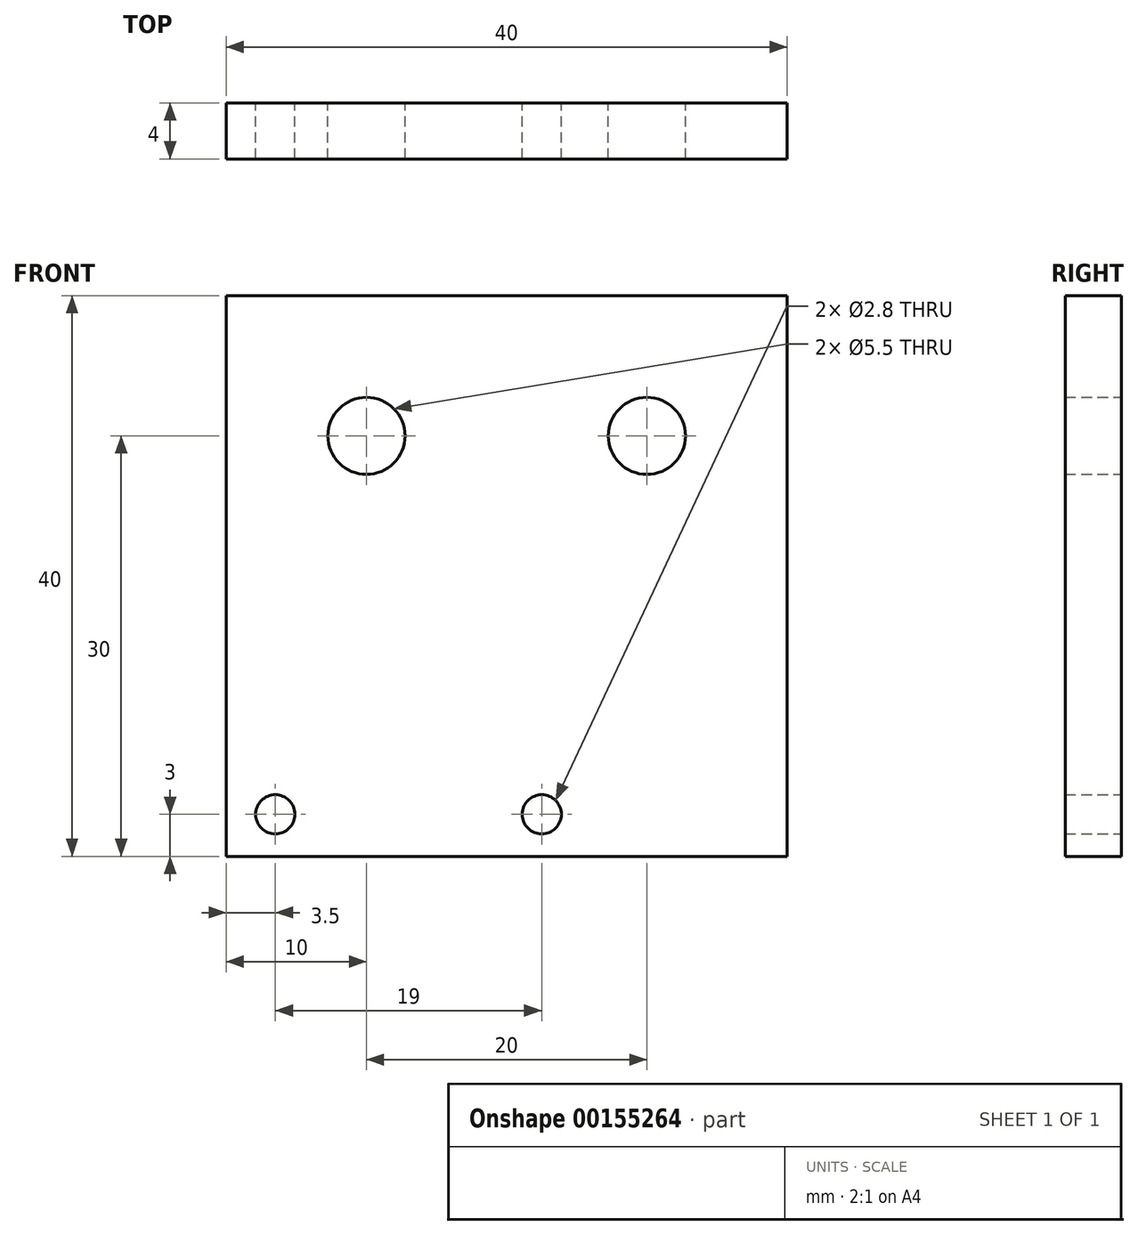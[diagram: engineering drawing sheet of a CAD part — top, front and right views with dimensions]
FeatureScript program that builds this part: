
annotation { "Feature Type Name" : "Feature", "Feature Type Description" : "" }
export const myFeature = defineFeature(function(context is Context, id is Id, definition is map)
    precondition{}
    {
        {
            var Q0;
            Q0=qCreatedBy(makeId("Front.planeOp"),FACE);
            var sketch = newSketch(context, id + "F0", { "sketchPlane" : qUnion([Q0])});
            skLineSegment(sketch, "E0.bottom", {"start": v(0, 0) * mm, "end": v(40, 0) * mm});
            skLineSegment(sketch, "E0.top", {"start": v(0, 40) * mm, "end": v(40, 40) * mm});
            skLineSegment(sketch, "E0.left", {"start": v(0, 0) * mm, "end": v(0, 40) * mm});
            skLineSegment(sketch, "E0.right", {"start": v(40, 0) * mm, "end": v(40, 40) * mm});
            skLineSegment(sketch, "E1", {"start": v(0, 30) * mm, "end": v(40, 30) * mm, "construction": true});
            skCircle(sketch, "E2", {"center": v(10, 30) * mm, "radius": 2.75 * mm});
            skCircle(sketch, "E3", {"center": v(30, 30) * mm, "radius": 2.75 * mm});
            skLineSegment(sketch, "E4", {"start": v(0, 3) * mm, "end": v(40, 3) * mm, "construction": true});
            skCircle(sketch, "E5", {"center": v(3.5, 3) * mm, "radius": 1.4 * mm});
            skCircle(sketch, "E6", {"center": v(22.5, 3) * mm, "radius": 1.4 * mm});
            skSolve(sketch);
        }
        {
            var Q0;
            Q0 = qSketchRegion(id + "F0", true);
            extrude(context, id + "F1", {"entities" : qUnion([Q0]), "depth" : 4 * mm});
        }
    });
